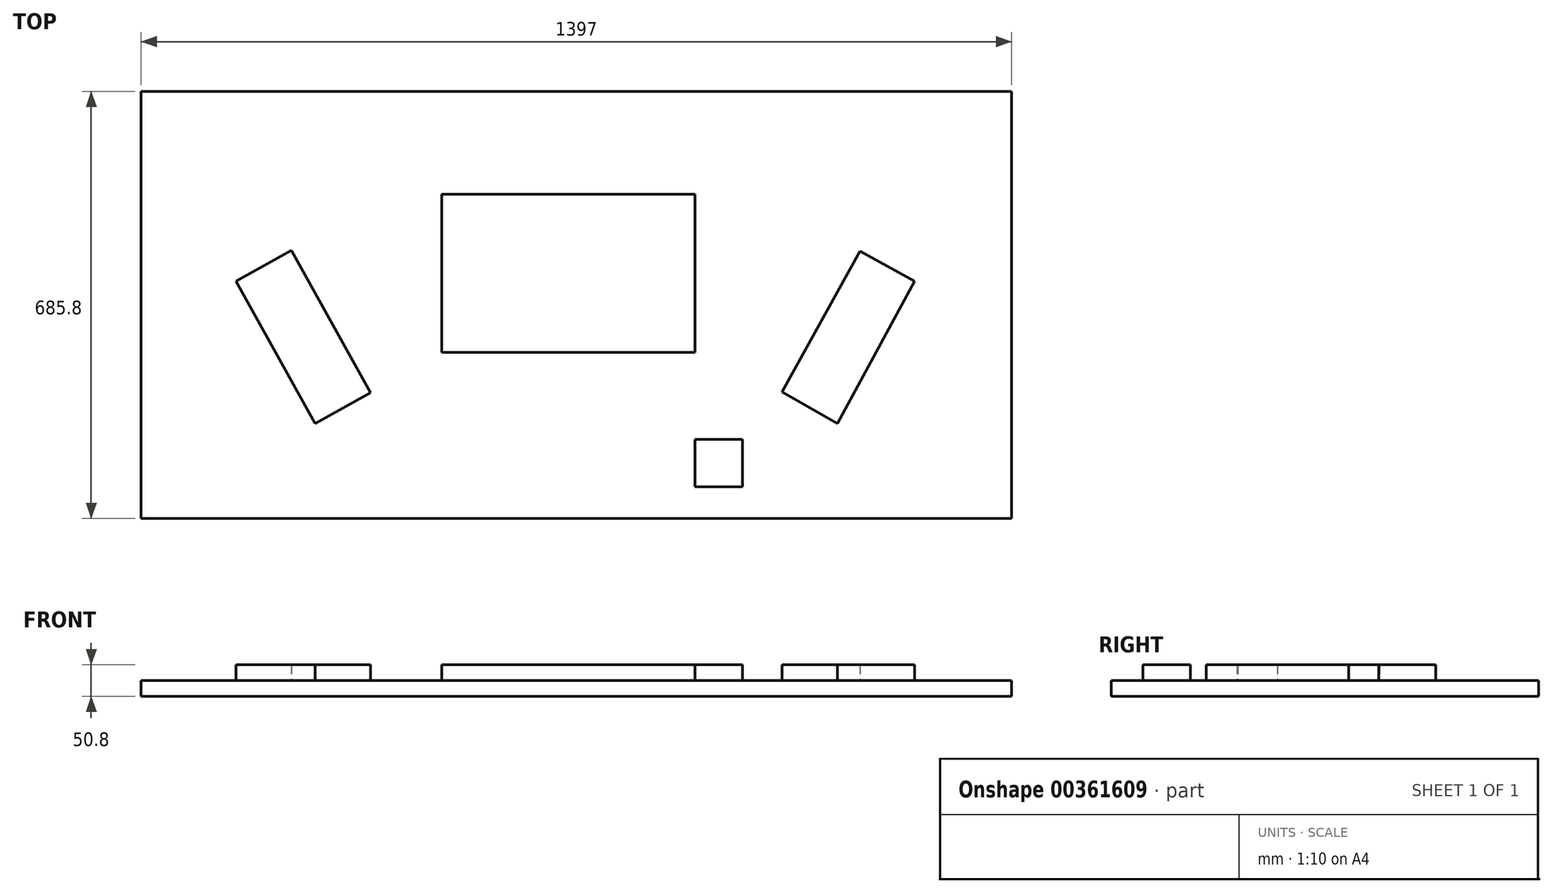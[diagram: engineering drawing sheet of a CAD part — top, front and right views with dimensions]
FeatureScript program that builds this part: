
annotation { "Feature Type Name" : "Feature", "Feature Type Description" : "" }
export const myFeature = defineFeature(function(context is Context, id is Id, definition is map)
    precondition{}
    {
        {
            var Q0;
            Q0=qCreatedBy(makeId("Top.planeOp"),FACE);
            var sketch = newSketch(context, id + "F0", { "sketchPlane" : qUnion([Q0])});
            skLineSegment(sketch, "E0.bottom", {"start": v(698.5, 342.9) * mm, "end": v(-698.5, 342.9) * mm});
            skLineSegment(sketch, "E0.top", {"start": v(698.5, -342.9) * mm, "end": v(-698.5, -342.9) * mm});
            skLineSegment(sketch, "E0.left", {"start": v(698.5, 342.9) * mm, "end": v(698.5, -342.9) * mm});
            skLineSegment(sketch, "E0.right", {"start": v(-698.5, 342.9) * mm, "end": v(-698.5, -342.9) * mm});
            skPoint(sketch, "E0.middle", {"position": v(0, 0) * mm});
            skSolve(sketch);
        }
        {
            var Q0;
            Q0 = qSketchRegion(id + "F0", true);
            extrude(context, id + "F1", {"entities" : qUnion([Q0]), "depth" : 25.4 * mm});
        }
        {
            var Q0;
            Q0=makeQuery(id+"F1.opExtrude","CAP_FACE",FACE,{"disambiguationData":[OSD([sQuery(id+"F0.wireOp",EDGE,"E0.bottom"),sQuery(id+"F0.wireOp",EDGE,"E0.top"),sQuery(id+"F0.wireOp",EDGE,"E0.left"),sQuery(id+"F0.wireOp",EDGE,"E0.right")])],"isStart":false});
            var sketch = newSketch(context, id + "F2", { "sketchPlane" : qUnion([Q0])});
            skLineSegment(sketch, "E1.bottom", {"start": v(317.5, -114.3) * mm, "end": v(-317.5, -114.3) * mm, "construction": true});
            skLineSegment(sketch, "E1.top", {"start": v(317.5, -190.5) * mm, "end": v(-317.5, -190.5) * mm, "construction": true});
            skLineSegment(sketch, "E1.left", {"start": v(317.5, -114.3) * mm, "end": v(317.5, -190.5) * mm, "construction": true});
            skLineSegment(sketch, "E1.right", {"start": v(-317.5, -114.3) * mm, "end": v(-317.5, -190.5) * mm, "construction": true});
            skPoint(sketch, "E1.middle", {"position": v(0, -152.4) * mm});
            skLineSegment(sketch, "E2.bottom", {"start": v(-330.2, -141.11) * mm, "end": v(-419.1, -190.5) * mm});
            skLineSegment(sketch, "E2.top", {"start": v(-457.2, 87.49) * mm, "end": v(-546.1, 38.1) * mm});
            skLineSegment(sketch, "E2.left", {"start": v(-330.2, -141.11) * mm, "end": v(-457.2, 87.49) * mm});
            skLineSegment(sketch, "E2.right", {"start": v(-419.1, -190.5) * mm, "end": v(-546.1, 38.1) * mm});
            skPoint(sketch, "E2.middle", {"position": v(-438.15, -51.5) * mm});
            skLineSegment(sketch, "E3.MirrorCS", {"start": v(330.2, -139.7) * mm, "end": v(455.33, 86.47) * mm});
            skLineSegment(sketch, "E4.MirrorCS", {"start": v(455.33, 86.47) * mm, "end": v(542.75, 38.1) * mm});
            skLineSegment(sketch, "E5.MirrorCS", {"start": v(419.1, -190.5) * mm, "end": v(542.75, 38.1) * mm});
            skLineSegment(sketch, "E6.MirrorCS", {"start": v(330.2, -139.7) * mm, "end": v(419.1, -190.5) * mm});
            skLineSegment(sketch, "E7.bottom", {"start": v(190.5, 177.8) * mm, "end": v(-215.9, 177.8) * mm});
            skLineSegment(sketch, "E7.top", {"start": v(190.5, -76.2) * mm, "end": v(-215.9, -76.2) * mm});
            skLineSegment(sketch, "E7.left", {"start": v(190.5, 177.8) * mm, "end": v(190.5, -76.2) * mm});
            skLineSegment(sketch, "E7.right", {"start": v(-215.9, 177.8) * mm, "end": v(-215.9, -76.2) * mm});
            skPoint(sketch, "E7.middle", {"position": v(0, 0) * mm});
            skLineSegment(sketch, "E8.bottom", {"start": v(190.5, -292.1) * mm, "end": v(266.7, -292.1) * mm});
            skLineSegment(sketch, "E8.top", {"start": v(190.5, -215.9) * mm, "end": v(266.7, -215.9) * mm});
            skLineSegment(sketch, "E8.left", {"start": v(190.5, -292.1) * mm, "end": v(190.5, -215.9) * mm});
            skLineSegment(sketch, "E8.right", {"start": v(266.7, -292.1) * mm, "end": v(266.7, -215.9) * mm});
            skPoint(sketch, "E8.middle", {"position": v(228.6, -254) * mm});
            skLineSegment(sketch, "E9", {"start": v(190.5, -292.1) * mm, "end": v(266.7, -215.9) * mm});
            skLineSegment(sketch, "E10", {"start": v(266.7, -292.1) * mm, "end": v(190.5, -215.9) * mm});
            skPoint(sketch, "E11", {"position": v(436.13, -54.78) * mm});
            skPoint(sketch, "E12", {"position": v(0, 50.8) * mm});
            skSolve(sketch);
        }
        {
            var Q0;
            Q0 = qSketchRegion(id + "F2", true);
            extrude(context, id + "F3", {"entities" : qUnion([Q0]), "depth" : 25.4 * mm});
        }
    });
